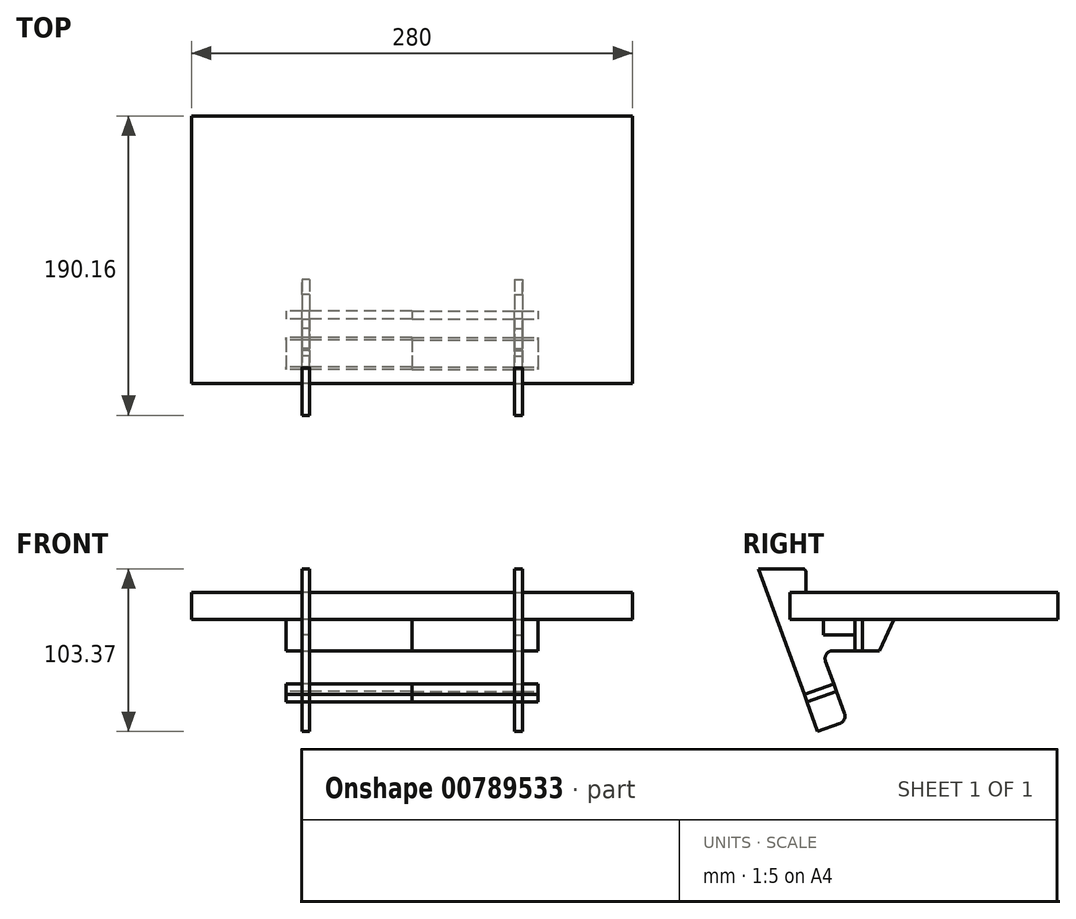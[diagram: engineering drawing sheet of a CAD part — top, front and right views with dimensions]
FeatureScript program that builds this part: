
annotation { "Feature Type Name" : "Feature", "Feature Type Description" : "" }
export const myFeature = defineFeature(function(context is Context, id is Id, definition is map)
    precondition{}
    {
        {
            var Q0;
            Q0=qCreatedBy(makeId("Top.planeOp"),FACE);
            var sketch = newSketch(context, id + "F0", { "sketchPlane" : qUnion([Q0])});
            skLineSegment(sketch, "E0.bottom", {"start": v(140, -85) * mm, "end": v(-140, -85) * mm});
            skLineSegment(sketch, "E0.top", {"start": v(140, 85) * mm, "end": v(-140, 85) * mm});
            skLineSegment(sketch, "E0.left", {"start": v(140, -85) * mm, "end": v(140, 85) * mm});
            skLineSegment(sketch, "E0.right", {"start": v(-140, -85) * mm, "end": v(-140, 85) * mm});
            skPoint(sketch, "E0.middle", {"position": v(0, 0) * mm});
            skSolve(sketch);
        }
        {
            var Q0;
            Q0=makeQuery(id+"F0.imprint","IMPRINT",FACE,{"disambiguationData":[TD([[makeQuery(id+"F0.imprint","IMPRINT",EDGE,{"derivedFrom":sQuery(id+"F0.wireOp",EDGE,"E0.bottom")}),-1.0]])]});
            extrude(context, id + "F1", {"entities" : qUnion([Q0]), "depth" : 17 * mm, "offsetDistance" : 25 * mm});
        }
        {
            var Q0;
            Q0=makeQuery(id+"F1.opExtrude","CAP_EDGE",EDGE,{"disambiguationData":[OSD([sQuery(id+"F0.wireOp",EDGE,"E0.bottom")])],"isStart":true});
            var Q1;
            Q1=qCreatedBy(makeId("Front.planeOp"),FACE);
            cPlane(context, id + "F2", {"entities" : qUnion([Q0, Q1]), "cplaneType" : CPlaneType.LINE_ANGLE, "offset" : 25 * mm, "angle" : 20 * degree, "oppositeDirection" : true, "width" : 150 * mm, "height" : 150 * mm});
        }
        {
            var Q0;
            Q0=qCreatedBy(id+"F2.planeOp",FACE);
            var sketch = newSketch(context, id + "F3", { "sketchPlane" : qUnion([Q0])});
            skLineSegment(sketch, "E1.bottom", {"start": v(70, 87.7) * mm, "end": v(65, 87.7) * mm});
            skLineSegment(sketch, "E1.top", {"start": v(70, -112.3) * mm, "end": v(65, -112.3) * mm});
            skLineSegment(sketch, "E1.left", {"start": v(70, 87.7) * mm, "end": v(70, -112.3) * mm});
            skLineSegment(sketch, "E1.right", {"start": v(65, 87.7) * mm, "end": v(65, -112.3) * mm});
            skSolve(sketch);
        }
        {
            var Q0;
            Q0=qSketchRegion(id+"F3",true);
            extrude(context, id + "F4", {"entities" : qUnion([Q0]), "oppositeDirection" : true, "depth" : 8 * mm, "offsetDistance" : 25 * mm, "hasSecondDirection" : true, "secondDirectionOppositeDirection" : false, "secondDirectionDepth" : 130 * mm});
        }
        {
            var Q0;
            Q0=makeQuery(id+"F1.opExtrude","SWEPT_BODY",BODY,{"disambiguationData":[OSD([sQuery(id+"F0.wireOp",EDGE,"E0.bottom"),sQuery(id+"F0.wireOp",EDGE,"E0.top"),sQuery(id+"F0.wireOp",EDGE,"E0.left"),sQuery(id+"F0.wireOp",EDGE,"E0.right")])]});
            var Q1;
            Q1=makeQuery(id+"F4.opExtrude","SWEPT_BODY",BODY,{"disambiguationData":[OSD([sQuery(id+"F3.wireOp",EDGE,"E1.bottom"),sQuery(id+"F3.wireOp",EDGE,"E1.top"),sQuery(id+"F3.wireOp",EDGE,"E1.left"),sQuery(id+"F3.wireOp",EDGE,"E1.right")])]});
            booleanBodies(context, id + "F5", {"operationType" : BooleanOperationType.SUBTRACTION, "tools" : qUnion([Q0]), "targets" : qUnion([Q1])});
        }
        {
            var Q0;
            Q0=makeQuery(id+"F4.opExtrude","SWEPT_FACE",FACE,{"disambiguationData":[OSD([sQuery(id+"F3.wireOp",EDGE,"E1.left")])]});
            var sketch = newSketch(context, id + "F6", { "sketchPlane" : qUnion([Q0])});
            skLineSegment(sketch, "E2.0", {"start": v(-31.06, 32) * mm, "end": v(164.2, 32) * mm});
            skLineSegment(sketch, "E3", {"start": v(48.9, -64.09) * mm, "end": v(19.02, 0) * mm});
            skLineSegment(sketch, "E4", {"start": v(19.02, 0) * mm, "end": v(84.8, -23.94) * mm, "construction": true});
            skLineSegment(sketch, "E5", {"start": v(75, 32) * mm, "end": v(75, 17) * mm});
            skLineSegment(sketch, "E6", {"start": v(67.54, -71.37) * mm, "end": v(48.74, -64.53) * mm});
            skLineSegment(sketch, "E7", {"start": v(48.74, -64.53) * mm, "end": v(48.9, -64.09) * mm});
            skPoint(sketch, "E8", {"position": v(105.16, 32) * mm});
            skPoint(sketch, "E9", {"position": v(15.83, 0) * mm});
            skSolve(sketch);
        }
        {
            var Q0;
            {var subQ0=sQuery(id+"F3.wireOp",EDGE,"E1.left");var subQ2=sQuery(id+"F3.wireOp",EDGE,"E1.bottom");var subQ3=makeQuery(id+"F4.opExtrude","SWEPT_EDGE",EDGE,{"disambiguationData":[OSD([subQ2,subQ0])]});Q0=makeQuery(id+"F6.imprint","IMPRINT",FACE,{"disambiguationData":[TD([[makeQuery(id+"F6.imprint","IMPRINT",EDGE,{"derivedFrom":subQ3}),1.0]])]});}
            var Q1;
            {var subQ0=sQuery(id+"F6.wireOp",EDGE,"E5");Q1=makeQuery(id+"F6.imprint","IMPRINT",FACE,{"disambiguationData":[TD([[makeQuery(id+"F6.imprint","IMPRINT",EDGE,{"derivedFrom":subQ0}),-1.0]])]});}
            var Q2;
            {var subQ2=sQuery(id+"F3.wireOp",EDGE,"E1.left");var subQ3=sQuery(id+"F3.wireOp",EDGE,"E1.top");var subQ8=makeQuery(id+"F4.opExtrude","SWEPT_EDGE",EDGE,{"disambiguationData":[OSD([subQ3,subQ2])]});Q2=makeQuery(id+"F6.imprint","IMPRINT",FACE,{"disambiguationData":[TD([[makeQuery(id+"F6.imprint","IMPRINT",EDGE,{"derivedFrom":subQ8}),-1.0]])]});}
            extrude(context, id + "F7", {"entities" : qUnion([Q0, Q1, Q2]), "operationType" : NewBodyOperationType.REMOVE, "oppositeDirection" : true, "depth" : 25 * mm, "offsetDistance" : 25 * mm});
        }
        {
            var Q0;
            Q0=makeQuery(id+"F4.opExtrude","SWEPT_FACE",FACE,{"disambiguationData":[OSD([sQuery(id+"F3.wireOp",EDGE,"E1.left")])]});
            var sketch = newSketch(context, id + "F8", { "sketchPlane" : qUnion([Q0])});
            skLineSegment(sketch, "E10.0", {"start": v(28.35, -20) * mm, "end": v(64.95, -20) * mm});
            skLineSegment(sketch, "E11.0", {"start": v(92.62, 56.03) * mm, "end": v(42, -83.04) * mm});
            skLineSegment(sketch, "E12.0", {"start": v(48.9, -64.09) * mm, "end": v(19.02, 0) * mm});
            skSolve(sketch);
        }
        {
            var Q0;
            {var subQ0=sQuery(id+"F8.wireOp",EDGE,"E10.0");Q0=makeQuery(id+"F8.imprint","IMPRINT",FACE,{"disambiguationData":[TD([[makeQuery(id+"F8.imprint","IMPRINT",EDGE,{"derivedFrom":subQ0}),-1.0]])]});}
            var Q1;
            Q1=makeQuery(id+"F4.opExtrude","SWEPT_FACE",FACE,{"disambiguationData":[OSD([sQuery(id+"F3.wireOp",EDGE,"E1.right")])]});
            extrude(context, id + "F9", {"entities" : qUnion([Q0]), "operationType" : NewBodyOperationType.REMOVE, "endBound" : BoundingType.UP_TO_SURFACE, "oppositeDirection" : true, "depth" : 25 * mm, "endBoundEntityFace" : qUnion([Q1]), "offsetDistance" : 25 * mm});
        }
        {
            var Q0;
            Q0=makeQuery(id+"F9.boolean.opBoolean","COPY",EDGE,{"derivedFrom":makeQuery(id+"F9.opExtrude","SWEPT_EDGE",EDGE,{"disambiguationData":[OSD([sQuery(id+"F8.wireOp",EDGE,"E10.0"),sQuery(id+"F8.wireOp",EDGE,"E11.0")])]})});
            var Q1;
            Q1=makeQuery(id+"F7.boolean.opBoolean","COPY",EDGE,{"derivedFrom":makeQuery(id+"F7.opExtrude","SWEPT_EDGE",EDGE,{"disambiguationData":[OSD([sQuery(id+"F3.wireOp",EDGE,"E1.left"),sQuery(id+"F6.wireOp",EDGE,"E2.0")])]})});
            var Q2;
            Q2=makeQuery(id+"F9.boolean.opBoolean","COPY",EDGE,{"derivedFrom":makeQuery(id+"F9.opExtrude","SWEPT_EDGE",EDGE,{"disambiguationData":[OSD([sQuery(id+"F8.wireOp",EDGE,"E10.0"),sQuery(id+"F8.wireOp",EDGE,"E12.0")])]})});
            var Q3;
            Q3=makeQuery(id+"F7.boolean.opBoolean","COPY",EDGE,{"derivedFrom":makeQuery(id+"F7.opExtrude","SWEPT_EDGE",EDGE,{"disambiguationData":[OSD([sQuery(id+"F6.wireOp",EDGE,"E6"),sQuery(id+"F6.wireOp",EDGE,"E7")])]})});
            fillet(context, id + "F10", {"entities" : qUnion([Q0, Q1, Q2, Q3]), "radius" : 5 * mm, "tangentPropagation" : true, "allowEdgeOverflow" : false});
        }
        {
            var Q0;
            Q0=makeQuery(id+"F4.opExtrude","SWEPT_FACE",FACE,{"disambiguationData":[OSD([sQuery(id+"F3.wireOp",EDGE,"E1.right")])]});
            var sketch = newSketch(context, id + "F11", { "sketchPlane" : qUnion([Q0])});
            skLineSegment(sketch, "E13.bottom", {"start": v(-76.09, -47.87) * mm, "end": v(-74.38, -52.57) * mm});
            skLineSegment(sketch, "E13.top", {"start": v(-57.3, -41.03) * mm, "end": v(-55.58, -45.73) * mm});
            skLineSegment(sketch, "E13.left", {"start": v(-57.3, -41.03) * mm, "end": v(-76.09, -47.87) * mm});
            skLineSegment(sketch, "E13.right", {"start": v(-55.58, -45.73) * mm, "end": v(-74.38, -52.57) * mm});
            skLineSegment(sketch, "E14.bottom", {"start": v(-39.02, 0) * mm, "end": v(-44.02, 0) * mm});
            skLineSegment(sketch, "E14.top", {"start": v(-39.02, -20) * mm, "end": v(-44.02, -20) * mm});
            skLineSegment(sketch, "E14.left", {"start": v(-39.02, 0) * mm, "end": v(-39.02, -20) * mm});
            skLineSegment(sketch, "E14.right", {"start": v(-44.02, 0) * mm, "end": v(-44.02, -20) * mm});
            skSolve(sketch);
        }
        {
            var Q0;
            Q0=qSketchRegion(id+"F11",true);
            var Q1;
            Q1=qCreatedBy(makeId("Right.planeOp"),FACE);
            var Q2;
            Q2=makeQuery(id+"F4.opExtrude","SWEPT_FACE",FACE,{"disambiguationData":[OSD([sQuery(id+"F3.wireOp",EDGE,"E1.left")])]});
            extrude(context, id + "F12", {"entities" : qUnion([Q0]), "endBound" : BoundingType.UP_TO_SURFACE, "depth" : 25 * mm, "endBoundEntityFace" : qUnion([Q1]), "offsetDistance" : 25 * mm, "hasSecondDirection" : true, "secondDirectionBound" : BoundingType.UP_TO_SURFACE, "secondDirectionOppositeDirection" : true, "secondDirectionDepth" : 17.8 * mm, "secondDirectionBoundEntityFace" : qUnion([Q2]), "hasSecondDirectionOffset" : true, "secondDirectionOffsetDistance" : 10 * mm, "secondDirectionOffsetOppositeDirection" : true});
        }
        {
            var Q0;
            Q0=makeQuery(id+"F12.opExtrude","SWEPT_FACE",FACE,{"disambiguationData":[OSD([sQuery(id+"F11.wireOp",EDGE,"E14.left")])]});
            var sketch = newSketch(context, id + "F13", { "sketchPlane" : qUnion([Q0])});
            skLineSegment(sketch, "E15", {"start": v(65, 0) * mm, "end": v(65, -20) * mm});
            skLineSegment(sketch, "E16", {"start": v(70, 0) * mm, "end": v(70, -20) * mm});
            skLineSegment(sketch, "E17", {"start": v(65, -10) * mm, "end": v(70, -10) * mm});
            skLineSegment(sketch, "E18", {"start": v(65, 0) * mm, "end": v(70, 0) * mm});
            skLineSegment(sketch, "E19", {"start": v(70, -20) * mm, "end": v(65, -20) * mm});
            skSolve(sketch);
        }
        {
            var Q0;
            {var subQ3=sQuery(id+"F13.wireOp",EDGE,"E17");Q0=makeQuery(id+"F13.imprint","IMPRINT",FACE,{"disambiguationData":[TD([[makeQuery(id+"F13.imprint","IMPRINT",EDGE,{"derivedFrom":subQ3}),1.0]])]});}
            extrude(context, id + "F14", {"entities" : qUnion([Q0]), "operationType" : NewBodyOperationType.REMOVE, "oppositeDirection" : true, "depth" : 25 * mm, "offsetDistance" : 25 * mm});
        }
        {
            var Q0;
            {var subQ3=sQuery(id+"F13.wireOp",EDGE,"E17");Q0=makeQuery(id+"F13.imprint","IMPRINT",FACE,{"disambiguationData":[TD([[makeQuery(id+"F13.imprint","IMPRINT",EDGE,{"derivedFrom":subQ3}),-1.0]])]});}
            var Q1;
            Q1=makeQuery(id+"F12.opExtrude","SWEPT_FACE",FACE,{"disambiguationData":[OSD([sQuery(id+"F11.wireOp",EDGE,"E14.right")])]});
            extrude(context, id + "F15", {"entities" : qUnion([Q0]), "operationType" : NewBodyOperationType.REMOVE, "endBound" : BoundingType.UP_TO_SURFACE, "oppositeDirection" : true, "depth" : 25 * mm, "endBoundEntityFace" : qUnion([Q1]), "offsetDistance" : 25 * mm});
        }
        {
            var Q0;
            Q0=makeQuery(id+"F12.opExtrude","SWEPT_FACE",FACE,{"disambiguationData":[OSD([sQuery(id+"F11.wireOp",EDGE,"E13.left")])]});
            var sketch = newSketch(context, id + "F16", { "sketchPlane" : qUnion([Q0])});
            skLineSegment(sketch, "E20", {"start": v(-65, -87.87) * mm, "end": v(-65, -67.87) * mm});
            skLineSegment(sketch, "E21", {"start": v(-70, -87.87) * mm, "end": v(-70, -67.87) * mm});
            skLineSegment(sketch, "E22", {"start": v(-65, -77.87) * mm, "end": v(-70, -77.87) * mm});
            skLineSegment(sketch, "E23", {"start": v(-65, -77.87) * mm, "end": v(-65, -87.87) * mm});
            skLineSegment(sketch, "E24", {"start": v(-65, -87.87) * mm, "end": v(-70, -87.87) * mm});
            skLineSegment(sketch, "E25", {"start": v(-70, -67.87) * mm, "end": v(-65, -67.87) * mm});
            skSolve(sketch);
        }
        {
            var Q0;
            {var subQ2=sQuery(id+"F16.wireOp",EDGE,"E22");Q0=makeQuery(id+"F16.imprint","IMPRINT",FACE,{"disambiguationData":[TD([[makeQuery(id+"F16.imprint","IMPRINT",EDGE,{"derivedFrom":subQ2}),1.0]])]});}
            var Q1;
            Q1=makeQuery(id+"F12.opExtrude","SWEPT_FACE",FACE,{"disambiguationData":[OSD([sQuery(id+"F11.wireOp",EDGE,"E13.right")])]});
            extrude(context, id + "F17", {"entities" : qUnion([Q0]), "operationType" : NewBodyOperationType.REMOVE, "endBound" : BoundingType.UP_TO_SURFACE, "oppositeDirection" : true, "depth" : 25 * mm, "endBoundEntityFace" : qUnion([Q1]), "offsetDistance" : 25 * mm});
        }
        {
            var Q0;
            {var subQ3=sQuery(id+"F16.wireOp",EDGE,"E22");Q0=makeQuery(id+"F16.imprint","IMPRINT",FACE,{"disambiguationData":[TD([[makeQuery(id+"F16.imprint","IMPRINT",EDGE,{"derivedFrom":subQ3}),-1.0]])]});}
            var Q1;
            Q1=makeQuery(id+"F12.opExtrude","SWEPT_FACE",FACE,{"disambiguationData":[OSD([sQuery(id+"F11.wireOp",EDGE,"E13.right")])]});
            extrude(context, id + "F18", {"entities" : qUnion([Q0]), "operationType" : NewBodyOperationType.REMOVE, "endBound" : BoundingType.UP_TO_SURFACE, "oppositeDirection" : true, "depth" : 25 * mm, "endBoundEntityFace" : qUnion([Q1]), "offsetDistance" : 25 * mm});
        }
        {
            var Q0;
            Q0=makeQuery(id+"F7.boolean.opBoolean","COPY",EDGE,{"derivedFrom":makeQuery(id+"F7.opExtrude","SWEPT_EDGE",EDGE,{"disambiguationData":[OSD([sQuery(id+"F6.wireOp",EDGE,"E2.0"),sQuery(id+"F6.wireOp",EDGE,"E5")])]})});
            var Q1;
            Q1=makeQuery(id+"F7.boolean.opBoolean","COPY",EDGE,{"derivedFrom":makeQuery(id+"F7.opExtrude","SWEPT_EDGE",EDGE,{"disambiguationData":[OSD([sQuery(id+"F0.wireOp",EDGE,"E0.bottom"),sQuery(id+"F0.wireOp",EDGE,"E0.top"),sQuery(id+"F0.wireOp",EDGE,"E0.left"),sQuery(id+"F0.wireOp",EDGE,"E0.right"),sQuery(id+"F3.wireOp",EDGE,"E1.left"),sQuery(id+"F6.wireOp",EDGE,"E3")])]})});
            var Q2;
            Q2=makeQuery(id+"F7.boolean.opBoolean","COPY",EDGE,{"derivedFrom":makeQuery(id+"F7.opExtrude","SWEPT_EDGE",EDGE,{"disambiguationData":[OSD([sQuery(id+"F3.wireOp",EDGE,"E1.left"),sQuery(id+"F6.wireOp",EDGE,"E6")])]})});
            var Q3;
            Q3=makeQuery(id+"F7.boolean.opBoolean","COPY",EDGE,{"derivedFrom":makeQuery(id+"F7.opExtrude","SWEPT_EDGE",EDGE,{"disambiguationData":[OSD([sQuery(id+"F0.wireOp",EDGE,"E0.bottom"),sQuery(id+"F0.wireOp",EDGE,"E0.top"),sQuery(id+"F0.wireOp",EDGE,"E0.left"),sQuery(id+"F0.wireOp",EDGE,"E0.right"),sQuery(id+"F3.wireOp",EDGE,"E1.left"),sQuery(id+"F6.wireOp",EDGE,"E5")])]})});
            fillet(context, id + "F19", {"entities" : qUnion([Q0, Q1, Q2, Q3]), "radius" : 2 * mm, "tangentPropagation" : true, "allowEdgeOverflow" : false});
        }
        {
            var Q0;
            Q0=makeQuery(id+"F4.opExtrude","SWEPT_BODY",BODY,{"disambiguationData":[OSD([sQuery(id+"F3.wireOp",EDGE,"E1.bottom"),sQuery(id+"F3.wireOp",EDGE,"E1.top"),sQuery(id+"F3.wireOp",EDGE,"E1.left"),sQuery(id+"F3.wireOp",EDGE,"E1.right")])]});
            var Q1;
            Q1=qCreatedBy(makeId("Right.planeOp"),FACE);
            mirror(context, id + "F20", {"entities" : qUnion([Q0]), "mirrorPlane" : qUnion([Q1])});
        }
        {
            var Q0;
            Q0=makeQuery(id+"F12.opExtrude","SWEPT_BODY",BODY,{"disambiguationData":[OSD([sQuery(id+"F11.wireOp",EDGE,"E14.bottom"),sQuery(id+"F11.wireOp",EDGE,"E14.top"),sQuery(id+"F11.wireOp",EDGE,"E14.left"),sQuery(id+"F11.wireOp",EDGE,"E14.right")])]});
            var Q1;
            Q1=makeQuery(id+"F12.opExtrude","SWEPT_BODY",BODY,{"disambiguationData":[OSD([sQuery(id+"F11.wireOp",EDGE,"E13.bottom"),sQuery(id+"F11.wireOp",EDGE,"E13.top"),sQuery(id+"F11.wireOp",EDGE,"E13.left"),sQuery(id+"F11.wireOp",EDGE,"E13.right")])]});
            var Q2;
            Q2=qCreatedBy(makeId("Right.planeOp"),FACE);
            mirror(context, id + "F21", {"operationType" : NewBodyOperationType.ADD, "entities" : qUnion([Q0, Q1]), "mirrorPlane" : qUnion([Q2])});
        }
        {
            var Q0;
            Q0=qCreatedBy(makeId("Top.planeOp"),FACE);
            var sketch = newSketch(context, id + "F22", { "sketchPlane" : qUnion([Q0])});
            skLineSegment(sketch, "E26.bottom", {"start": v(140, -85) * mm, "end": v(-140, -85) * mm});
            skLineSegment(sketch, "E26.top", {"start": v(140, 85) * mm, "end": v(-140, 85) * mm});
            skLineSegment(sketch, "E26.left", {"start": v(140, -85) * mm, "end": v(140, 85) * mm});
            skLineSegment(sketch, "E26.right", {"start": v(-140, -85) * mm, "end": v(-140, 85) * mm});
            skPoint(sketch, "E26.middle", {"position": v(0, 0) * mm});
            skSolve(sketch);
        }
        {
            var Q0;
            Q0=makeQuery(id+"F22.imprint","IMPRINT",FACE,{"disambiguationData":[TD([[makeQuery(id+"F22.imprint","IMPRINT",EDGE,{"derivedFrom":sQuery(id+"F22.wireOp",EDGE,"E26.bottom")}),-1.0]])]});
            extrude(context, id + "F23", {"entities" : qUnion([Q0]), "depth" : 17 * mm, "offsetDistance" : 25 * mm});
        }
    });
